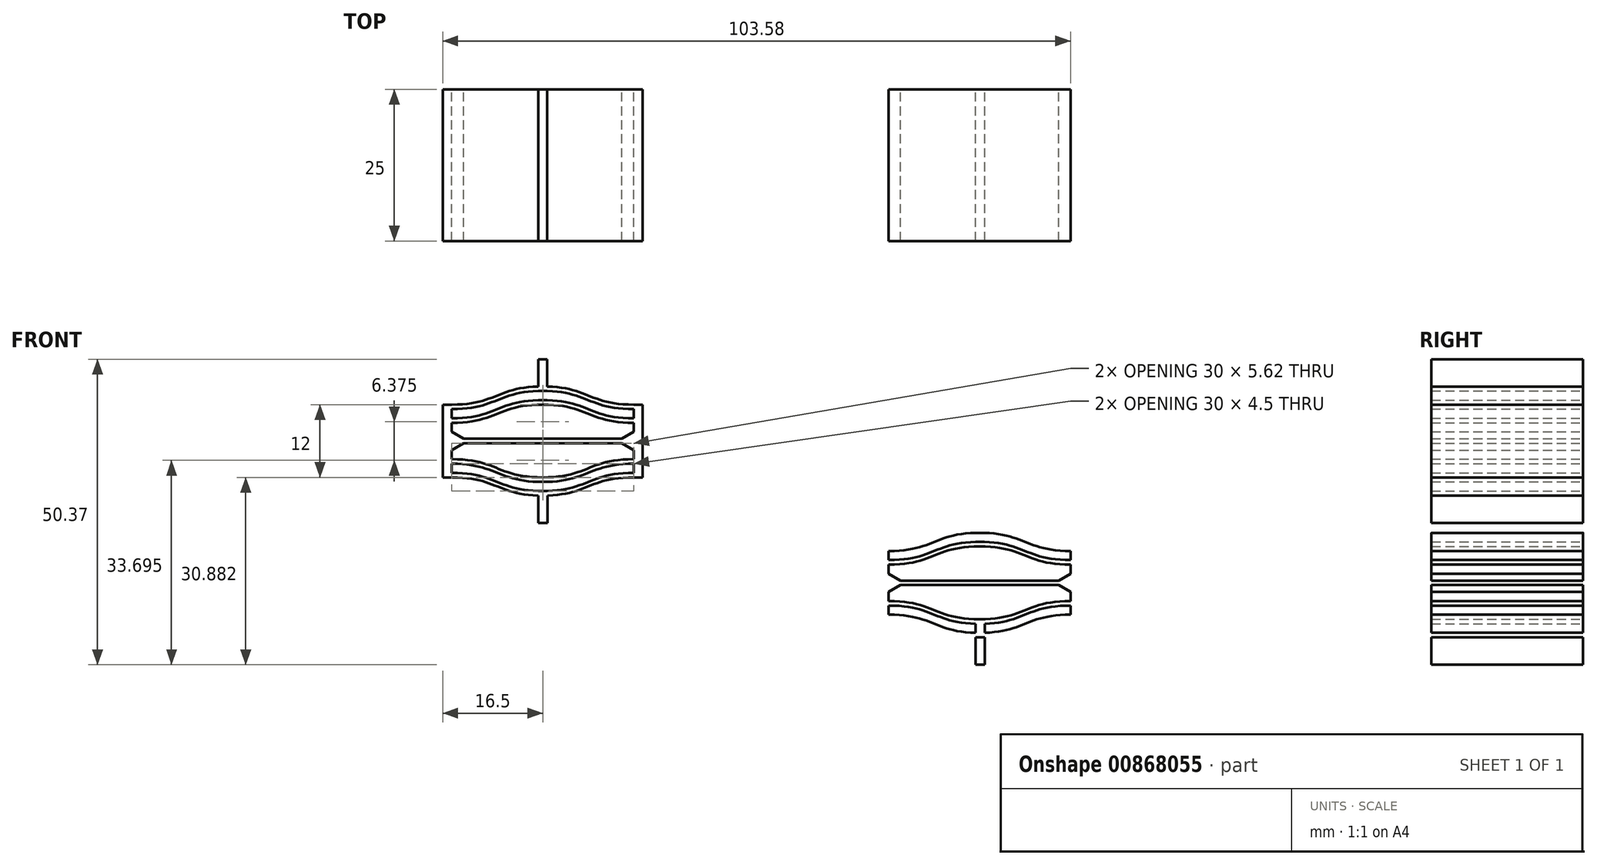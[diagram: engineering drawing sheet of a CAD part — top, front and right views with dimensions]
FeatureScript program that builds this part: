
annotation { "Feature Type Name" : "Feature", "Feature Type Description" : "" }
export const myFeature = defineFeature(function(context is Context, id is Id, definition is map)
    precondition{}
    {
        {
            var Q0;
            Q0=qCreatedBy(makeId("Front.planeOp"),FACE);
            var sketch = newSketch(context, id + "F0", { "sketchPlane" : qUnion([Q0])});
            skLineSegment(sketch, "E0", {"start": v(-72.08, 35.4) * mm, "end": v(-72.08, 23.4) * mm});
            skLineSegment(sketch, "E1", {"start": v(-39.08, 35.4) * mm, "end": v(-39.08, 23.4) * mm});
            skLineSegment(sketch, "E2", {"start": v(-72.08, 23.4) * mm, "end": v(-70.58, 23.4) * mm});
            skLineSegment(sketch, "E3", {"start": v(-72.08, 35.4) * mm, "end": v(-70.58, 35.4) * mm});
            skLineSegment(sketch, "E4", {"start": v(-39.08, 35.4) * mm, "end": v(-40.58, 35.4) * mm});
            skLineSegment(sketch, "E5", {"start": v(-39.08, 23.4) * mm, "end": v(-40.58, 23.4) * mm});
            skLineSegment(sketch, "E6", {"start": v(-70.58, 34.64) * mm, "end": v(-70.58, 33.14) * mm});
            skLineSegment(sketch, "E7", {"start": v(-40.58, 34.64) * mm, "end": v(-40.58, 33.14) * mm});
            skLineSegment(sketch, "E8", {"start": v(-70.58, 27.9) * mm, "end": v(-68.63, 29.02) * mm});
            skLineSegment(sketch, "E9", {"start": v(-70.58, 30.9) * mm, "end": v(-68.63, 29.77) * mm});
            skPoint(sketch, "E10", {"position": v(-40.58, 27.9) * mm});
            skPoint(sketch, "E11", {"position": v(-40.58, 30.9) * mm});
            skLineSegment(sketch, "E12", {"start": v(-40.58, 30.9) * mm, "end": v(-42.53, 29.77) * mm});
            skLineSegment(sketch, "E13", {"start": v(-42.53, 29.02) * mm, "end": v(-40.58, 27.9) * mm});
            skPoint(sketch, "E14.positionSnap0", {"position": v(-55.58, 29.77) * mm});
            skPoint(sketch, "E15", {"position": v(-70.58, 34.64) * mm});
            skPoint(sketch, "E16", {"position": v(-70.58, 24.14) * mm});
            skPoint(sketch, "E17", {"position": v(-70.58, 33.14) * mm});
            skPoint(sketch, "E18", {"position": v(-70.58, 32.4) * mm});
            skPoint(sketch, "E19", {"position": v(-70.58, 25.64) * mm});
            skPoint(sketch, "E20", {"position": v(-70.58, 26.4) * mm});
            skPoint(sketch, "E21", {"position": v(-40.58, 34.64) * mm});
            skPoint(sketch, "E22", {"position": v(-40.58, 33.14) * mm});
            skPoint(sketch, "E23", {"position": v(-40.58, 32.4) * mm});
            skPoint(sketch, "E24", {"position": v(-40.58, 26.4) * mm});
            skPoint(sketch, "E25", {"position": v(-40.58, 25.64) * mm});
            skPoint(sketch, "E26", {"position": v(-40.58, 24.14) * mm});
            skLineSegment(sketch, "E27.trimOffspring", {"start": v(-68.63, 29.77) * mm, "end": v(-55.58, 29.77) * mm});
            skLineSegment(sketch, "E28.trimOffspring", {"start": v(-68.63, 29.02) * mm, "end": v(-42.53, 29.02) * mm});
            skLineSegment(sketch, "E29.trimOffspring", {"start": v(-70.58, 32.4) * mm, "end": v(-70.58, 30.9) * mm});
            skLineSegment(sketch, "E30.trimOffspring", {"start": v(-70.58, 25.64) * mm, "end": v(-70.58, 24.14) * mm});
            skLineSegment(sketch, "E31.trimOffspring", {"start": v(-40.58, 32.4) * mm, "end": v(-40.58, 30.9) * mm});
            skLineSegment(sketch, "E32.trimOffspring", {"start": v(-40.58, 25.64) * mm, "end": v(-40.58, 24.14) * mm});
            skLineSegment(sketch, "E33.trimOffspring", {"start": v(-70.58, 27.9) * mm, "end": v(-70.58, 26.4) * mm});
            skLineSegment(sketch, "E34.trimOffspring", {"start": v(-40.58, 27.9) * mm, "end": v(-40.58, 26.4) * mm});
            skLineSegment(sketch, "E35", {"start": v(-55.58, 29.77) * mm, "end": v(-42.53, 29.77) * mm});
            skPoint(sketch, "E36", {"position": v(-55.58, 32.4) * mm});
            skPoint(sketch, "E37", {"position": v(-55.58, 35.4) * mm});
            skPoint(sketch, "E38", {"position": v(-63.08, 32.4) * mm});
            skPoint(sketch, "E39", {"position": v(-63.08, 33.9) * mm});
            skPoint(sketch, "E40", {"position": v(-48.08, 33.9) * mm});
            skFitSpline(sketch, "E41", {"points": [v(-70.58, 32.4) * mm, v(-63.08, 33.9) * mm, v(-55.58, 35.4) * mm], "startDerivative": vector(22.5, 0) * mm, "endDerivative": vector(22.5, 0) * mm});
            skFitSpline(sketch, "E42", {"points": [v(-55.58, 35.4) * mm, v(-48.08, 33.9) * mm, v(-40.58, 32.4) * mm], "startDerivative": vector(22.5, 0) * mm, "endDerivative": vector(22.5, 0) * mm});
            skFitSpline(sketch, "E43", {"points": [v(-70.58, 33.14) * mm, v(-63.08, 34.64) * mm, v(-55.58, 36.14) * mm], "startDerivative": vector(22.5, 0) * mm, "endDerivative": vector(22.5, 0) * mm});
            skFitSpline(sketch, "E44", {"points": [v(-55.58, 36.14) * mm, v(-48.08, 34.64) * mm, v(-40.58, 33.14) * mm], "startDerivative": vector(22.5, 0) * mm, "endDerivative": vector(22.5, 0) * mm});
            skFitSpline(sketch, "E45", {"points": [v(-70.58, 34.64) * mm, v(-63.08, 36.14) * mm, v(-55.58, 37.64) * mm], "startDerivative": vector(22.5, 0) * mm, "endDerivative": vector(22.5, 0) * mm});
            skFitSpline(sketch, "E46", {"points": [v(-55.58, 37.64) * mm, v(-48.08, 36.14) * mm, v(-40.58, 34.64) * mm], "startDerivative": vector(22.5, 0) * mm, "endDerivative": vector(22.5, 0) * mm});
            skFitSpline(sketch, "E47", {"points": [v(-70.58, 35.4) * mm, v(-63.08, 36.9) * mm, v(-55.58, 38.4) * mm], "startDerivative": vector(22.5, 0) * mm, "endDerivative": vector(22.5, 0) * mm});
            skFitSpline(sketch, "E48", {"points": [v(-55.58, 38.4) * mm, v(-48.08, 36.9) * mm, v(-40.58, 35.4) * mm], "startDerivative": vector(22.5, 0) * mm, "endDerivative": vector(22.5, 0) * mm});
            skFitSpline(sketch, "E49", {"points": [v(-40.58, 26.4) * mm, v(-48.08, 24.9) * mm, v(-55.58, 23.4) * mm], "startDerivative": vector(-22.5, 0) * mm, "endDerivative": vector(-22.5, 0) * mm});
            skFitSpline(sketch, "E50", {"points": [v(-55.58, 23.4) * mm, v(-63.08, 24.9) * mm, v(-70.58, 26.4) * mm], "startDerivative": vector(-22.5, 0) * mm, "endDerivative": vector(-22.5, 0) * mm});
            skFitSpline(sketch, "E51", {"points": [v(-40.58, 25.64) * mm, v(-48.08, 24.14) * mm, v(-55.58, 22.64) * mm], "startDerivative": vector(-22.5, 0) * mm, "endDerivative": vector(-22.5, 0) * mm});
            skFitSpline(sketch, "E52", {"points": [v(-55.58, 22.64) * mm, v(-63.08, 24.14) * mm, v(-70.58, 25.64) * mm], "startDerivative": vector(-22.5, 0) * mm, "endDerivative": vector(-22.5, 0) * mm});
            skFitSpline(sketch, "E53", {"points": [v(-40.58, 24.14) * mm, v(-48.08, 22.64) * mm, v(-55.58, 21.14) * mm], "startDerivative": vector(-22.5, 0) * mm, "endDerivative": vector(-22.5, 0) * mm});
            skFitSpline(sketch, "E54", {"points": [v(-55.58, 21.14) * mm, v(-63.08, 22.64) * mm, v(-70.58, 24.14) * mm], "startDerivative": vector(-22.5, 0) * mm, "endDerivative": vector(-22.5, 0) * mm});
            skFitSpline(sketch, "E55", {"points": [v(-40.58, 23.4) * mm, v(-48.08, 21.9) * mm, v(-55.58, 20.4) * mm], "startDerivative": vector(-22.5, 0) * mm, "endDerivative": vector(-22.5, 0) * mm});
            skFitSpline(sketch, "E56", {"points": [v(-55.58, 20.4) * mm, v(-63.08, 21.9) * mm, v(-70.58, 23.4) * mm], "startDerivative": vector(-22.5, 0) * mm, "endDerivative": vector(-22.5, 0) * mm});
            skPoint(sketch, "E57", {"position": v(-56.33, 23.05) * mm});
            skPoint(sketch, "E58", {"position": v(-54.83, 23.05) * mm});
            skLineSegment(sketch, "E59", {"start": v(-56.33, 22.65) * mm, "end": v(-56.33, 21.15) * mm});
            skLineSegment(sketch, "E60", {"start": v(-54.83, 22.65) * mm, "end": v(-54.83, 21.15) * mm});
            skLineSegment(sketch, "E61", {"start": v(-54.83, 21.15) * mm, "end": v(-54.76, 21.1) * mm});
            skLineSegment(sketch, "E62", {"start": v(-56.33, 20.4) * mm, "end": v(-56.33, 15.9) * mm});
            skLineSegment(sketch, "E63", {"start": v(-56.33, 15.9) * mm, "end": v(-54.76, 15.9) * mm});
            skLineSegment(sketch, "E64", {"start": v(-54.76, 15.9) * mm, "end": v(-54.76, 20.4) * mm});
            skLineSegment(sketch, "E65", {"start": v(-56.33, 36.13) * mm, "end": v(-56.33, 37.63) * mm});
            skLineSegment(sketch, "E66", {"start": v(-56.33, 38.38) * mm, "end": v(-56.33, 42.88) * mm});
            skLineSegment(sketch, "E67", {"start": v(-56.33, 42.88) * mm, "end": v(-54.83, 42.88) * mm});
            skLineSegment(sketch, "E68", {"start": v(-54.83, 37.63) * mm, "end": v(-54.83, 36.13) * mm});
            skPoint(sketch, "E69.end.orphan", {"position": v(-54.83, 38.4) * mm});
            skLineSegment(sketch, "E70", {"start": v(-54.83, 42.88) * mm, "end": v(-54.83, 38.38) * mm});
            skPoint(sketch, "E71", {"position": v(-56.33, 23.4) * mm});
            skPoint(sketch, "E72", {"position": v(-54.83, 23.4) * mm});
            skLineSegment(sketch, "E73", {"start": v(0, 12) * mm, "end": v(0, 0) * mm});
            skLineSegment(sketch, "E74", {"start": v(33, 12) * mm, "end": v(33, 0) * mm});
            skLineSegment(sketch, "E75", {"start": v(0, 0) * mm, "end": v(1.5, 0) * mm});
            skLineSegment(sketch, "E76", {"start": v(0, 12) * mm, "end": v(1.5, 12) * mm});
            skLineSegment(sketch, "E77", {"start": v(33, 12) * mm, "end": v(31.5, 12) * mm});
            skLineSegment(sketch, "E78", {"start": v(33, 0) * mm, "end": v(31.5, 0) * mm});
            skLineSegment(sketch, "E79", {"start": v(1.5, 11.25) * mm, "end": v(1.5, 9.75) * mm});
            skLineSegment(sketch, "E80", {"start": v(31.5, 11.25) * mm, "end": v(31.5, 9.75) * mm});
            skLineSegment(sketch, "E81", {"start": v(1.5, 4.5) * mm, "end": v(3.45, 5.63) * mm});
            skLineSegment(sketch, "E82", {"start": v(1.5, 7.5) * mm, "end": v(3.45, 6.38) * mm});
            skPoint(sketch, "E83", {"position": v(31.5, 4.5) * mm});
            skPoint(sketch, "E84", {"position": v(31.5, 7.5) * mm});
            skLineSegment(sketch, "E85", {"start": v(31.5, 7.5) * mm, "end": v(29.55, 6.38) * mm});
            skLineSegment(sketch, "E86", {"start": v(29.55, 5.63) * mm, "end": v(31.5, 4.5) * mm});
            skPoint(sketch, "E87.positionSnap0", {"position": v(16.5, 6.38) * mm});
            skPoint(sketch, "E88", {"position": v(1.5, 11.25) * mm});
            skPoint(sketch, "E89", {"position": v(1.5, 0.75) * mm});
            skPoint(sketch, "E90", {"position": v(1.5, 9.75) * mm});
            skPoint(sketch, "E91", {"position": v(1.5, 9) * mm});
            skPoint(sketch, "E92", {"position": v(1.5, 2.25) * mm});
            skPoint(sketch, "E93", {"position": v(1.5, 3) * mm});
            skPoint(sketch, "E94", {"position": v(31.5, 11.25) * mm});
            skPoint(sketch, "E95", {"position": v(31.5, 9.75) * mm});
            skPoint(sketch, "E96", {"position": v(31.5, 9) * mm});
            skPoint(sketch, "E97", {"position": v(31.5, 3) * mm});
            skPoint(sketch, "E98", {"position": v(31.5, 2.25) * mm});
            skPoint(sketch, "E99", {"position": v(31.5, 0.75) * mm});
            skLineSegment(sketch, "E100.trimOffspring", {"start": v(3.45, 6.37) * mm, "end": v(16.5, 6.38) * mm});
            skLineSegment(sketch, "E101.trimOffspring", {"start": v(3.45, 5.62) * mm, "end": v(29.55, 5.63) * mm});
            skLineSegment(sketch, "E102.trimOffspring", {"start": v(1.5, 9) * mm, "end": v(1.5, 7.5) * mm});
            skLineSegment(sketch, "E103.trimOffspring", {"start": v(1.5, 2.25) * mm, "end": v(1.5, 0.75) * mm});
            skLineSegment(sketch, "E104.trimOffspring", {"start": v(31.5, 9) * mm, "end": v(31.5, 7.5) * mm});
            skLineSegment(sketch, "E105.trimOffspring", {"start": v(31.5, 2.25) * mm, "end": v(31.5, 0.75) * mm});
            skLineSegment(sketch, "E106.trimOffspring", {"start": v(1.5, 4.5) * mm, "end": v(1.5, 3) * mm});
            skLineSegment(sketch, "E107.trimOffspring", {"start": v(31.5, 4.5) * mm, "end": v(31.5, 3) * mm});
            skLineSegment(sketch, "E108", {"start": v(16.5, 6.38) * mm, "end": v(29.55, 6.38) * mm});
            skPoint(sketch, "E109", {"position": v(16.5, 9) * mm});
            skPoint(sketch, "E110", {"position": v(16.5, 12) * mm});
            skPoint(sketch, "E111", {"position": v(9, 9) * mm});
            skPoint(sketch, "E112", {"position": v(9, 10.5) * mm});
            skPoint(sketch, "E113", {"position": v(24, 10.5) * mm});
            skFitSpline(sketch, "E114", {"points": [v(1.5, 9) * mm, v(9, 10.5) * mm, v(16.5, 12) * mm], "startDerivative": vector(22.5, 0) * mm, "endDerivative": vector(22.5, 0) * mm});
            skFitSpline(sketch, "E115", {"points": [v(16.5, 12) * mm, v(24, 10.5) * mm, v(31.5, 9) * mm], "startDerivative": vector(22.5, 0) * mm, "endDerivative": vector(22.5, 0) * mm});
            skFitSpline(sketch, "E116", {"points": [v(1.5, 9.75) * mm, v(9, 11.25) * mm, v(16.5, 12.75) * mm], "startDerivative": vector(22.5, 0) * mm, "endDerivative": vector(22.5, 0) * mm});
            skFitSpline(sketch, "E117", {"points": [v(16.5, 12.75) * mm, v(24, 11.25) * mm, v(31.5, 9.75) * mm], "startDerivative": vector(22.5, 0) * mm, "endDerivative": vector(22.5, 0) * mm});
            skFitSpline(sketch, "E118", {"points": [v(1.5, 11.25) * mm, v(9, 12.75) * mm, v(16.5, 14.25) * mm], "startDerivative": vector(22.5, 0) * mm, "endDerivative": vector(22.5, 0) * mm});
            skFitSpline(sketch, "E119", {"points": [v(16.5, 14.25) * mm, v(24, 12.75) * mm, v(31.5, 11.25) * mm], "startDerivative": vector(22.5, 0) * mm, "endDerivative": vector(22.5, 0) * mm});
            skFitSpline(sketch, "E120", {"points": [v(1.5, 12) * mm, v(9, 13.5) * mm, v(16.5, 15) * mm], "startDerivative": vector(22.5, 0) * mm, "endDerivative": vector(22.5, 0) * mm});
            skFitSpline(sketch, "E121", {"points": [v(16.64, 15) * mm, v(24.14, 13.5) * mm, v(31.64, 12) * mm], "startDerivative": vector(22.5, 0) * mm, "endDerivative": vector(22.5, 0) * mm});
            skFitSpline(sketch, "E122", {"points": [v(31.5, 3) * mm, v(24, 1.5) * mm, v(16.5, 0) * mm], "startDerivative": vector(-22.5, 0) * mm, "endDerivative": vector(-22.5, 0) * mm});
            skFitSpline(sketch, "E123", {"points": [v(16.5, 0) * mm, v(9, 1.5) * mm, v(1.5, 3) * mm], "startDerivative": vector(-22.5, 0) * mm, "endDerivative": vector(-22.5, 0) * mm});
            skFitSpline(sketch, "E124", {"points": [v(31.5, 2.25) * mm, v(24, 0.75) * mm, v(16.57, -0.75) * mm], "startDerivative": vector(-22.5, 0) * mm, "endDerivative": vector(-22.5, 0) * mm});
            skFitSpline(sketch, "E125", {"points": [v(16.5, -0.75) * mm, v(9, 0.75) * mm, v(1.5, 2.25) * mm], "startDerivative": vector(-22.5, 0) * mm, "endDerivative": vector(-22.5, 0) * mm});
            skFitSpline(sketch, "E126", {"points": [v(31.5, 0.75) * mm, v(24, -0.75) * mm, v(16.5, -2.25) * mm], "startDerivative": vector(-22.5, 0) * mm, "endDerivative": vector(-22.5, 0) * mm});
            skFitSpline(sketch, "E127", {"points": [v(16.5, -2.25) * mm, v(9, -0.75) * mm, v(1.5, 0.75) * mm], "startDerivative": vector(-22.5, 0) * mm, "endDerivative": vector(-22.5, 0) * mm});
            skFitSpline(sketch, "E128", {"points": [v(31.5, 0) * mm, v(24, -1.5) * mm, v(16.5, -3) * mm], "startDerivative": vector(-22.5, 0) * mm, "endDerivative": vector(-22.5, 0) * mm});
            skFitSpline(sketch, "E129", {"points": [v(16.64, -3) * mm, v(9.14, -1.5) * mm, v(1.64, 0) * mm], "startDerivative": vector(-22.5, 0) * mm, "endDerivative": vector(-22.5, 0) * mm});
            skPoint(sketch, "E130", {"position": v(15.82, -0.34) * mm});
            skPoint(sketch, "E131", {"position": v(17.32, -0.34) * mm});
            skLineSegment(sketch, "E132", {"start": v(15.82, -0.74) * mm, "end": v(15.82, -2.24) * mm});
            skLineSegment(sketch, "E133", {"start": v(17.32, -0.74) * mm, "end": v(17.32, -2.24) * mm});
            skLineSegment(sketch, "E134", {"start": v(15.82, -2.99) * mm, "end": v(15.82, -7.49) * mm});
            skLineSegment(sketch, "E135", {"start": v(15.82, 12.74) * mm, "end": v(15.82, 14.24) * mm});
            skLineSegment(sketch, "E136", {"start": v(15.82, 15) * mm, "end": v(15.82, 19.5) * mm});
            skLineSegment(sketch, "E137", {"start": v(17.25, 14.24) * mm, "end": v(17.25, 12.74) * mm});
            skPoint(sketch, "E138.end.orphan", {"position": v(17.25, 15) * mm});
            skPoint(sketch, "E139", {"position": v(15.82, 0) * mm});
            skPoint(sketch, "E140", {"position": v(17.32, 0.01) * mm});
            skLineSegment(sketch, "E141", {"start": v(15.82, -7.49) * mm, "end": v(17.32, -7.49) * mm});
            skLineSegment(sketch, "E142", {"start": v(17.32, -7.49) * mm, "end": v(17.32, -2.99) * mm});
            skLineSegment(sketch, "E143", {"start": v(17.25, 14.24) * mm, "end": v(17.25, 15) * mm});
            skLineSegment(sketch, "E144", {"start": v(17.25, 15) * mm, "end": v(17.25, 19.5) * mm});
            skLineSegment(sketch, "E145", {"start": v(15.82, 19.5) * mm, "end": v(17.25, 19.5) * mm});
            skSolve(sketch);
        }
        {
            var Q0;
            Q0 = qSketchRegion(id + "F0", true);
            extrude(context, id + "F1", {"entities" : qUnion([Q0]), "depth" : 25 * mm, "offsetDistance" : 25 * mm});
        }
    });
